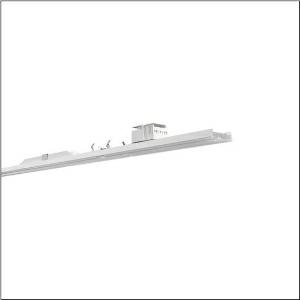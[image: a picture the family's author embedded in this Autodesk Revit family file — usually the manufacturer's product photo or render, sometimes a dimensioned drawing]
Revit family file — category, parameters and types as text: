
# Revit family: licross_r__11_recessed_ho_51tl18cn4cxl_517b
name_source: partatom
category: Lighting Fixtures
units: mm (PartAtom-declared; Revit-internal decimal feet)

## family parameters
Cut with Voids When Loaded = No
Host = Face
Light Source = No
Part Type = Normal
Room Calculation Point = No
Round Connector Dimension = Use Diameter
Shared = No

## types (1)
- --- (1 x LED, 12000 lm, 68.8 W, 4000K)
    Apparent Load = 69 VA
    CIE Flux Codes = 78 94 99 100 100
    Color Rendering = 80
    Color Temperature = 4000K
    Default Elevation = 1800 mm
    Description = Licross® 11 Recessed HOluminaire insert, length: 1.500mm, width: 66mm, height: 67mm, LED rated luminous flux: 12.000lm, light colour: 840, control gear: ON/OFF Multilumen, CLOi, control gear: ECG Multilumen, with plug, 3-pole, with phase selection, mains connection: 220..240V, AC, 50/60Hz, halogen-free wiring, primary optical cover: cover, of PMMA, light emission: direct distribution, protection rating (complete): IP40, insulation class (complete): insulation class I (protective earthing), certification: CE, ENEC, VDE, protection symbol: D if used in an environment without relevant dust loads with corresponding accessories, permissible ambient temperature for indoor applications: -35..+35°C, reducing of maximum allowable ambient temperature of 5°C with ceiling mounting, corresponds to IFS (International Featured Standards) requirements for safety and quality in the food industry, packaging unit: 1 piece
    Height = 58 mm
    Lamp = 1 x LED
    Lamp Light Flux = 12000 lm
    Lamp Power = 68.8 W
    Lamp count = 1
    Length = 1500 mm
    Luminous efficacy = 174 lm/W
    Manufacturer = Siteco
    ModVariant = No
    Model = 51TL18CN4CXL
    Mounting Place = Ceiling
    Mounting Type = Pendant
    Number of Poles = 1
    OnlyDefault = Yes
    Power Factor = 1
    Product Name = Licross® 11 Recessed HO
    Product group = luminaire insert
    ProductGroupID = 902
    Protection Class = Protection class I
    Protection Degree = IP 40
    RLX_Detail_Level = 1
    RlxData = <blob elided: 20089 chars, md5=5a182871>
    Socket = socket
    Standby Power = 0 W
    System Light Flux = 12000 lm
    System Power = 69 W
    Type Comments = factory setting: luminous flux: 100 % | (A | C | E) | 160 mA
    Type Image = l_1266722.jpg
    URL = http://relux.com
    VarID = @adj_138715
    Voltage = 0 V
    Weight = 0.00 kg
    Width = 66 mm

## geometry (parser evidence)
native form markers: Blend x4, Sweep x13
no freeform markers — native parametric forms only
